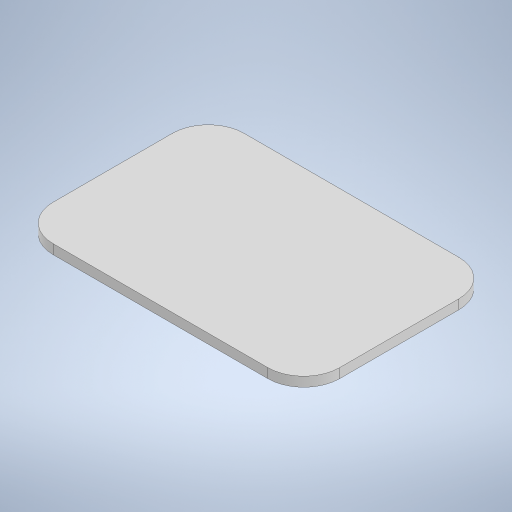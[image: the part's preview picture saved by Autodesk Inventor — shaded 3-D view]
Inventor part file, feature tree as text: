
AUTODESK INVENTOR PART (.ipt)
format: ipt  version: 2024.2 (Build 282272000, 272)  size: 211,968 bytes
history: native  units: in
note: dims shown in document units (in); Inventor stores cm internally (conversion verified against a paired STEP export)
features: extrude x1, sketch x1
ambient origin geometry x8: Origin, YZ Plane, XZ Plane, XY Plane, X Axis, Y Axis, Z Axis, Center Point
bodies: Solid1 (feature_tree)
feature tree (2):
  extrude  "Extrusion1"  Depth=3.0in
  sketch  "Sketch1"  dims[d0=2.0in d1=3.0in d2=0.375in d3=0.375in d4=0.1in d5=0.0in]
